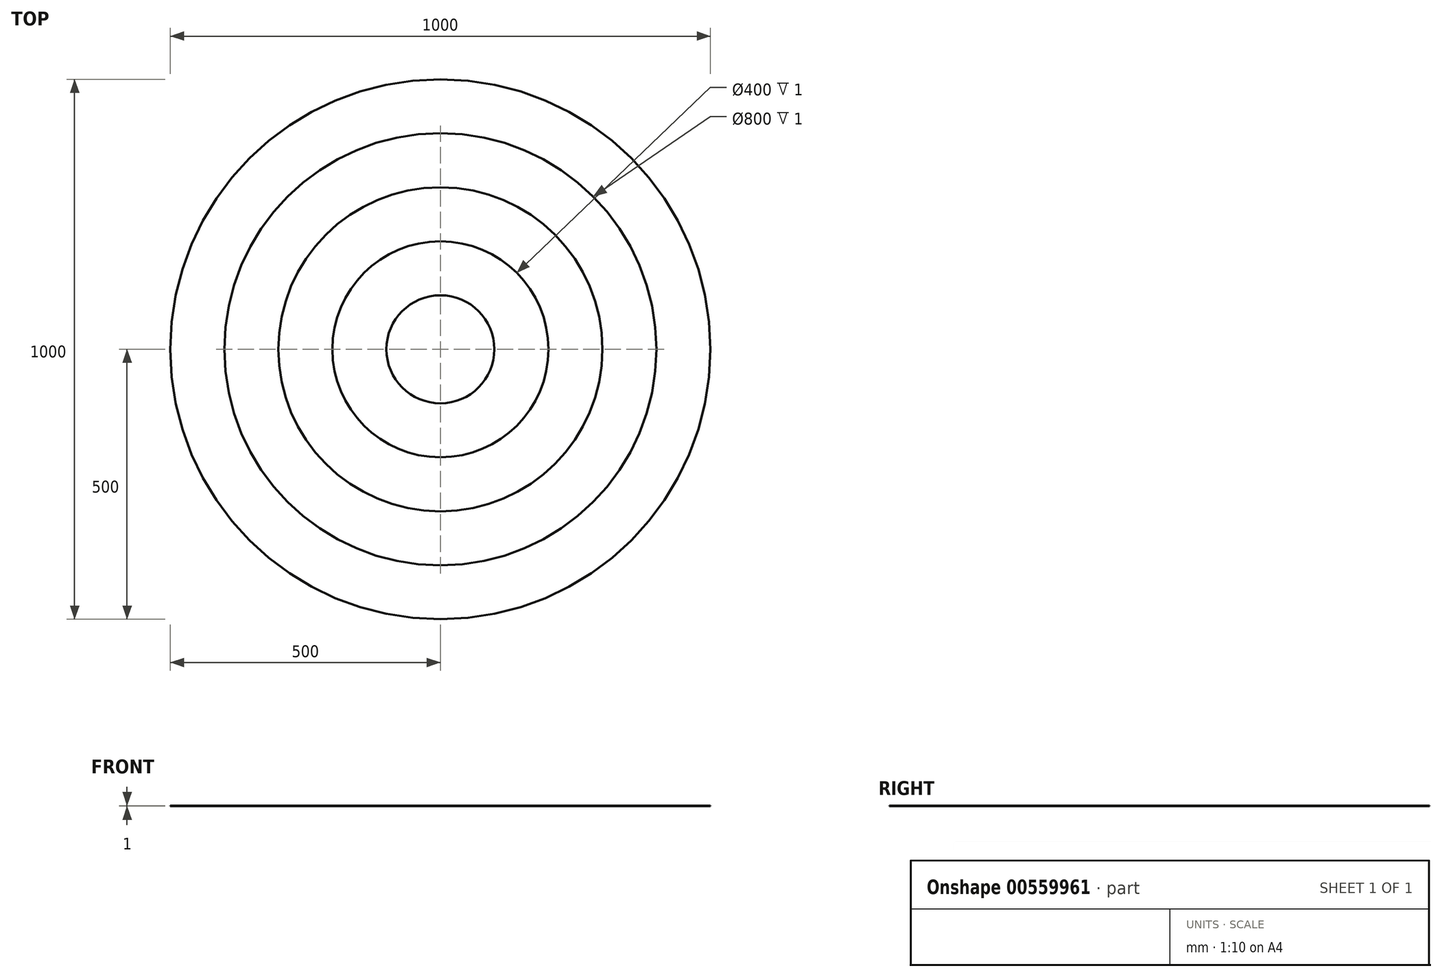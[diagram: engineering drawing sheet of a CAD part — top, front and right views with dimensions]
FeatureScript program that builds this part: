
annotation { "Feature Type Name" : "Feature", "Feature Type Description" : "" }
export const myFeature = defineFeature(function(context is Context, id is Id, definition is map)
    precondition{}
    {
        {
            var Q0;
            Q0=qCreatedBy(makeId("Top.planeOp"),FACE);
            var sketch = newSketch(context, id + "F0", { "sketchPlane" : qUnion([Q0])});
            skCircle(sketch, "E0", {"center": v(0, 0) * mm, "radius": 500 * mm});
            skCircle(sketch, "E1", {"center": v(0, 0) * mm, "radius": 400 * mm});
            skSolve(sketch);
        }
        {
            var Q0;
            Q0=qSketchRegion(id+"F0",true);
            extrude(context, id + "F1", {"entities" : qUnion([Q0]), "depth" : 1 * mm, "offsetDistance" : 25.4 * mm});
        }
        {
            var Q0;
            Q0=qCreatedBy(makeId("Top.planeOp"),FACE);
            var sketch = newSketch(context, id + "F2", { "sketchPlane" : qUnion([Q0])});
            skCircle(sketch, "E2", {"center": v(0, 0) * mm, "radius": 300 * mm});
            skCircle(sketch, "E3.0", {"center": v(0, 0) * mm, "radius": 200 * mm});
            skSolve(sketch);
        }
        {
            var Q0;
            Q0=qSketchRegion(id+"F2",true);
            var Q1;
            Q1=makeQuery(id+"F1.opExtrude","CAP_FACE",FACE,{"disambiguationData":[OSD([sQuery(id+"F0.wireOp",EDGE,"E0"),sQuery(id+"F0.wireOp",EDGE,"E1")])],"isStart":false});
            extrude(context, id + "F3", {"entities" : qUnion([Q0]), "depth" : 1 * mm, "endBoundEntityFace" : qUnion([Q1]), "offsetDistance" : 25.4 * mm});
        }
        {
            var Q0;
            Q0=qCreatedBy(makeId("Top.planeOp"),FACE);
            var sketch = newSketch(context, id + "F4", { "sketchPlane" : qUnion([Q0])});
            skCircle(sketch, "E4", {"center": v(0, 0) * mm, "radius": 100 * mm});
            skSolve(sketch);
        }
        {
            var Q0;
            Q0=qSketchRegion(id+"F4",true);
            extrude(context, id + "F5", {"entities" : qUnion([Q0]), "depth" : 1 * mm, "offsetDistance" : 25.4 * mm});
        }
    });
